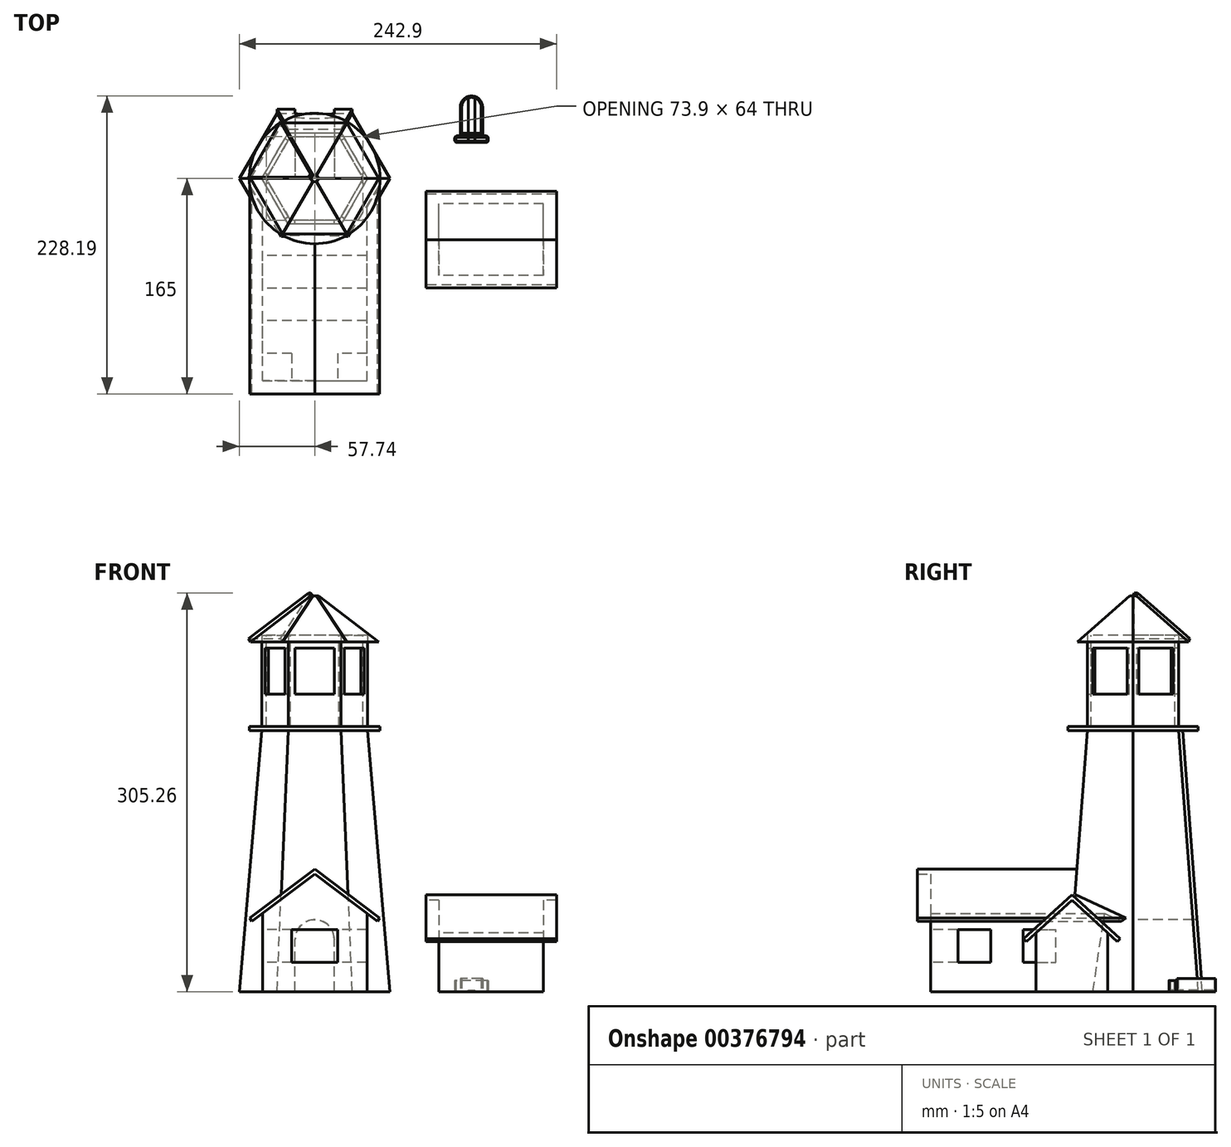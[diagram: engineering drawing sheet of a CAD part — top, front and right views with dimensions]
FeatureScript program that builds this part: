
annotation { "Feature Type Name" : "Feature", "Feature Type Description" : "" }
export const myFeature = defineFeature(function(context is Context, id is Id, definition is map)
    precondition{}
    {
        {
            var Q0;
            Q0=qCreatedBy(makeId("Top.planeOp"),FACE);
            var sketch = newSketch(context, id + "F0", { "sketchPlane" : qUnion([Q0])});
            skCircle(sketch, "E0.cCircle", {"center": v(0, 0) * mm, "radius": 50 * mm, "construction": true});
            skLineSegment(sketch, "E0.0", {"start": v(28.87, -50) * mm, "end": v(-28.87, -50) * mm});
            skLineSegment(sketch, "E0.1", {"start": v(-28.87, -50) * mm, "end": v(-57.74, 0) * mm});
            skLineSegment(sketch, "E0.2", {"start": v(-57.74, 0) * mm, "end": v(-28.87, 50) * mm});
            skLineSegment(sketch, "E0.3", {"start": v(-28.87, 50) * mm, "end": v(28.87, 50) * mm});
            skLineSegment(sketch, "E0.4", {"start": v(28.87, 50) * mm, "end": v(57.74, 0) * mm});
            skLineSegment(sketch, "E0.5", {"start": v(57.74, 0) * mm, "end": v(28.87, -50) * mm});
            skPoint(sketch, "E0.0.midPoint", {"position": v(0, -50) * mm});
            skSolve(sketch);
        }
        {
            var Q0;
            Q0=qCreatedBy(makeId("Top.planeOp"),FACE);
            cPlane(context, id + "F1", {"entities" : qUnion([Q0]), "cplaneType" : CPlaneType.OFFSET, "offset" : 200 * mm, "width" : 150 * mm, "height" : 150 * mm});
        }
        {
            var Q0;
            Q0=qCreatedBy(id+"F1.planeOp",FACE);
            var sketch = newSketch(context, id + "F2", { "sketchPlane" : qUnion([Q0])});
            skCircle(sketch, "E1.cCircle", {"center": v(0, 0) * mm, "radius": 35 * mm, "construction": true});
            skLineSegment(sketch, "E1.0", {"start": v(20.2, -35) * mm, "end": v(-20.2, -35) * mm});
            skLineSegment(sketch, "E1.1", {"start": v(-20.2, -35) * mm, "end": v(-40.41, 0) * mm});
            skLineSegment(sketch, "E1.2", {"start": v(-40.41, 0) * mm, "end": v(-20.2, 35) * mm});
            skLineSegment(sketch, "E1.3", {"start": v(-20.2, 35) * mm, "end": v(20.2, 35) * mm});
            skLineSegment(sketch, "E1.4", {"start": v(20.2, 35) * mm, "end": v(40.41, 0) * mm});
            skLineSegment(sketch, "E1.5", {"start": v(40.41, 0) * mm, "end": v(20.2, -35) * mm});
            skPoint(sketch, "E1.0.midPoint", {"position": v(0, -35) * mm});
            skSolve(sketch);
        }
        {
            var Q0;
            Q0=makeQuery(id+"F0.imprint","IMPRINT",FACE,{"disambiguationData":[TD([[makeQuery(id+"F0.imprint","IMPRINT",EDGE,{"derivedFrom":sQuery(id+"F0.wireOp",EDGE,"E0.0")}),-1.0]])]});
            var Q1;
            Q1=makeQuery(id+"F2.imprint","IMPRINT",FACE,{"disambiguationData":[TD([[makeQuery(id+"F2.imprint","IMPRINT",EDGE,{"derivedFrom":sQuery(id+"F2.wireOp",EDGE,"E1.0")}),-1.0]])]});
            loft(context, id + "F3", {"sheetProfilesArray" : [{ "sheetProfileEntities" : qUnion([Q0]) }, { "sheetProfileEntities" : qUnion([Q1]) }]});
        }
        {
            var Q0;
            Q0=makeQuery(id+"F3.opLoft","CAP_FACE",FACE,{"disambiguationData":[OSD([makeQuery(id+"F2.imprint","IMPRINT",FACE,{"disambiguationData":[TD([[makeQuery(id+"F2.imprint","IMPRINT",EDGE,{"derivedFrom":sQuery(id+"F2.wireOp",EDGE,"E1.0")}),-1.0]])]})])],"isStart":true});
            var sketch = newSketch(context, id + "F4", { "sketchPlane" : qUnion([Q0])});
            skCircle(sketch, "E2", {"center": v(0, 0) * mm, "radius": 50 * mm});
            skSolve(sketch);
        }
        {
            var Q0;
            Q0=makeQuery(id+"F4.imprint","IMPRINT",FACE,{"disambiguationData":[TD([[makeQuery(id+"F4.imprint","IMPRINT",EDGE,{"derivedFrom":sQuery(id+"F4.wireOp",EDGE,"E2")}),1.0]])]});
            var Q1;
            {var subQ2=sQuery(id+"F2.wireOp",EDGE,"E1.1");var subQ3=sQuery(id+"F2.wireOp",EDGE,"E1.0");var subQ4=sQuery(id+"F2.wireOp",EDGE,"E1.5");Q1=makeQuery(id+"F4.imprint","IMPRINT",FACE,{"disambiguationData":[TD([[makeQuery(id+"F4.imprint","IMPRINT",EDGE,{"derivedFrom":makeQuery(id+"F3.opLoft","MID_CAP_EDGE",EDGE,{"disambiguationData":[OSD([subQ3,subQ2,subQ4])],"capPos":1.0})}),1.0]])]});}
            extrude(context, id + "F5", {"entities" : qUnion([Q0, Q1]), "depth" : 3 * mm});
        }
        {
            var Q0;
            Q0=makeQuery(id+"F5.opExtrude","CAP_FACE",FACE,{"disambiguationData":[OSD([sQuery(id+"F4.wireOp",EDGE,"E2")])],"isStart":false});
            var sketch = newSketch(context, id + "F6", { "sketchPlane" : qUnion([Q0])});
            skCircle(sketch, "E3.cCircle", {"center": v(0, 0) * mm, "radius": 35 * mm, "construction": true});
            skLineSegment(sketch, "E3.0", {"start": v(20.2, -35) * mm, "end": v(-20.2, -35) * mm});
            skLineSegment(sketch, "E3.1", {"start": v(-20.2, -35) * mm, "end": v(-40.41, 0) * mm});
            skLineSegment(sketch, "E3.2", {"start": v(-40.41, 0) * mm, "end": v(-20.2, 35) * mm});
            skLineSegment(sketch, "E3.3", {"start": v(-20.2, 35) * mm, "end": v(20.2, 35) * mm});
            skLineSegment(sketch, "E3.4", {"start": v(20.2, 35) * mm, "end": v(40.41, 0) * mm});
            skLineSegment(sketch, "E3.5", {"start": v(40.41, 0) * mm, "end": v(20.2, -35) * mm});
            skPoint(sketch, "E3.0.midPoint", {"position": v(0, -35) * mm});
            skSolve(sketch);
        }
        {
            var Q0;
            Q0=makeQuery(id+"F6.imprint","IMPRINT",FACE,{"disambiguationData":[TD([[makeQuery(id+"F6.imprint","IMPRINT",EDGE,{"derivedFrom":sQuery(id+"F6.wireOp",EDGE,"E3.0")}),-1.0]])]});
            extrude(context, id + "F7", {"entities" : qUnion([Q0]), "depth" : 70 * mm});
        }
        {
            var Q0;
            Q0=makeQuery(id+"F7.opExtrude","CAP_FACE",FACE,{"disambiguationData":[OSD([sQuery(id+"F6.wireOp",EDGE,"E3.0"),sQuery(id+"F6.wireOp",EDGE,"E3.1"),sQuery(id+"F6.wireOp",EDGE,"E3.2"),sQuery(id+"F6.wireOp",EDGE,"E3.3"),sQuery(id+"F6.wireOp",EDGE,"E3.4"),sQuery(id+"F6.wireOp",EDGE,"E3.5")])],"isStart":false});
            var sketch = newSketch(context, id + "F8", { "sketchPlane" : qUnion([Q0])});
            skCircle(sketch, "E4.cCircle", {"center": v(0, 0) * mm, "radius": 32 * mm, "construction": true});
            skLineSegment(sketch, "E4.0", {"start": v(18.48, -32) * mm, "end": v(-18.48, -32) * mm});
            skLineSegment(sketch, "E4.1", {"start": v(-18.48, -32) * mm, "end": v(-36.95, 0) * mm});
            skLineSegment(sketch, "E4.2", {"start": v(-36.95, 0) * mm, "end": v(-18.48, 32) * mm});
            skLineSegment(sketch, "E4.3", {"start": v(-18.48, 32) * mm, "end": v(18.48, 32) * mm});
            skLineSegment(sketch, "E4.4", {"start": v(18.48, 32) * mm, "end": v(36.95, 0) * mm});
            skLineSegment(sketch, "E4.5", {"start": v(36.95, 0) * mm, "end": v(18.48, -32) * mm});
            skPoint(sketch, "E4.0.midPoint", {"position": v(0, -32) * mm});
            skSolve(sketch);
        }
        {
            var Q0;
            Q0=makeQuery(id+"F8.imprint","IMPRINT",FACE,{"disambiguationData":[TD([[makeQuery(id+"F8.imprint","IMPRINT",EDGE,{"derivedFrom":sQuery(id+"F8.wireOp",EDGE,"E4.0")}),-1.0]])]});
            var Q1;
            Q1=makeQuery(id+"F5.opExtrude","CAP_FACE",FACE,{"disambiguationData":[OSD([sQuery(id+"F4.wireOp",EDGE,"E2")])],"isStart":false});
            extrude(context, id + "F9", {"entities" : qUnion([Q0]), "operationType" : NewBodyOperationType.REMOVE, "endBound" : BoundingType.UP_TO_SURFACE, "oppositeDirection" : true, "endBoundEntityFace" : qUnion([Q1]), "depth" : 25 * mm});
        }
        {
            var Q0;
            Q0=makeQuery(id+"F7.opExtrude","CAP_FACE",FACE,{"disambiguationData":[OSD([sQuery(id+"F6.wireOp",EDGE,"E3.0"),sQuery(id+"F6.wireOp",EDGE,"E3.1"),sQuery(id+"F6.wireOp",EDGE,"E3.2"),sQuery(id+"F6.wireOp",EDGE,"E3.3"),sQuery(id+"F6.wireOp",EDGE,"E3.4"),sQuery(id+"F6.wireOp",EDGE,"E3.5")])],"isStart":false});
            var sketch = newSketch(context, id + "F10", { "sketchPlane" : qUnion([Q0])});
            skLineSegment(sketch, "E5", {"start": v(0, -32) * mm, "end": v(0, -35) * mm, "construction": true});
            skLineSegment(sketch, "E6.bottom", {"start": v(15.2, -35) * mm, "end": v(-15.2, -35) * mm});
            skLineSegment(sketch, "E6.top", {"start": v(15.2, -32) * mm, "end": v(-15.2, -32) * mm});
            skLineSegment(sketch, "E6.left", {"start": v(15.2, -35) * mm, "end": v(15.2, -32) * mm});
            skLineSegment(sketch, "E6.right", {"start": v(-15.2, -35) * mm, "end": v(-15.2, -32) * mm});
            skPoint(sketch, "E6.middle", {"position": v(0, -33.5) * mm});
            skLineSegment(sketch, "E7.1.0", {"start": v(35.32, -2.83) * mm, "end": v(20.1, -29.17) * mm});
            skLineSegment(sketch, "E7.1.1", {"start": v(37.91, -4.33) * mm, "end": v(35.32, -2.83) * mm});
            skLineSegment(sketch, "E7.1.2", {"start": v(37.91, -4.33) * mm, "end": v(22.7, -30.67) * mm});
            skLineSegment(sketch, "E7.1.3", {"start": v(22.7, -30.67) * mm, "end": v(20.1, -29.17) * mm});
            skLineSegment(sketch, "E7.2.0", {"start": v(20.1, 29.17) * mm, "end": v(35.32, 2.83) * mm});
            skLineSegment(sketch, "E7.2.1", {"start": v(22.7, 30.67) * mm, "end": v(20.1, 29.17) * mm});
            skLineSegment(sketch, "E7.2.2", {"start": v(22.7, 30.67) * mm, "end": v(37.91, 4.33) * mm});
            skLineSegment(sketch, "E7.2.3", {"start": v(37.91, 4.33) * mm, "end": v(35.32, 2.83) * mm});
            skLineSegment(sketch, "E7.3.0", {"start": v(-15.2, 32) * mm, "end": v(15.2, 32) * mm});
            skLineSegment(sketch, "E7.3.1", {"start": v(-15.2, 35) * mm, "end": v(-15.2, 32) * mm});
            skLineSegment(sketch, "E7.3.2", {"start": v(-15.2, 35) * mm, "end": v(15.2, 35) * mm});
            skLineSegment(sketch, "E7.3.3", {"start": v(15.2, 35) * mm, "end": v(15.2, 32) * mm});
            skLineSegment(sketch, "E7.4.0", {"start": v(-35.32, 2.83) * mm, "end": v(-20.1, 29.17) * mm});
            skLineSegment(sketch, "E7.4.1", {"start": v(-37.91, 4.33) * mm, "end": v(-35.32, 2.83) * mm});
            skLineSegment(sketch, "E7.4.2", {"start": v(-37.91, 4.33) * mm, "end": v(-22.7, 30.67) * mm});
            skLineSegment(sketch, "E7.4.3", {"start": v(-22.7, 30.67) * mm, "end": v(-20.1, 29.17) * mm});
            skLineSegment(sketch, "E7.5.0", {"start": v(-20.1, -29.17) * mm, "end": v(-35.32, -2.83) * mm});
            skLineSegment(sketch, "E7.5.1", {"start": v(-22.7, -30.67) * mm, "end": v(-20.1, -29.17) * mm});
            skLineSegment(sketch, "E7.5.2", {"start": v(-22.7, -30.67) * mm, "end": v(-37.91, -4.33) * mm});
            skLineSegment(sketch, "E7.5.3", {"start": v(-37.91, -4.33) * mm, "end": v(-35.32, -2.83) * mm});
            skPoint(sketch, "E7.center", {"position": v(0, 0) * mm});
            skSolve(sketch);
        }
        {
            var Q0;
            Q0 = qSketchRegion(id + "F10", true);
            extrude(context, id + "F11", {"entities" : qUnion([Q0]), "operationType" : NewBodyOperationType.REMOVE, "oppositeDirection" : true, "depth" : 45 * mm, "hasSecondDirection" : true, "secondDirectionOppositeDirection" : true, "secondDirectionDepth" : 10 * mm});
        }
        {
            var Q0;
            Q0=makeQuery(id+"F7.opExtrude","CAP_FACE",FACE,{"disambiguationData":[OSD([sQuery(id+"F6.wireOp",EDGE,"E3.0"),sQuery(id+"F6.wireOp",EDGE,"E3.1"),sQuery(id+"F6.wireOp",EDGE,"E3.2"),sQuery(id+"F6.wireOp",EDGE,"E3.3"),sQuery(id+"F6.wireOp",EDGE,"E3.4"),sQuery(id+"F6.wireOp",EDGE,"E3.5")])],"isStart":false});
            cPlane(context, id + "F12", {"entities" : qUnion([Q0]), "cplaneType" : CPlaneType.OFFSET, "offset" : 5 * mm, "oppositeDirection" : true, "width" : 150 * mm, "height" : 150 * mm});
        }
        {
            var Q0;
            Q0=qCreatedBy(id+"F12.planeOp",FACE);
            var sketch = newSketch(context, id + "F13", { "sketchPlane" : qUnion([Q0])});
            skCircle(sketch, "E8.cCircle", {"center": v(0, 0) * mm, "radius": 42.5 * mm, "construction": true});
            skLineSegment(sketch, "E8.0", {"start": v(24.54, -42.5) * mm, "end": v(-24.54, -42.5) * mm});
            skLineSegment(sketch, "E8.1", {"start": v(-24.54, -42.5) * mm, "end": v(-49.07, 0) * mm});
            skLineSegment(sketch, "E8.2", {"start": v(-49.07, 0) * mm, "end": v(-24.54, 42.5) * mm});
            skLineSegment(sketch, "E8.3", {"start": v(-24.54, 42.5) * mm, "end": v(24.54, 42.5) * mm});
            skLineSegment(sketch, "E8.4", {"start": v(24.54, 42.5) * mm, "end": v(49.07, 0) * mm});
            skLineSegment(sketch, "E8.5", {"start": v(49.07, 0) * mm, "end": v(24.54, -42.5) * mm});
            skPoint(sketch, "E8.0.midPoint", {"position": v(0, -42.5) * mm});
            skSolve(sketch);
        }
        {
            var Q0;
            Q0=qCreatedBy(id+"F12.planeOp",FACE);
            cPlane(context, id + "F14", {"entities" : qUnion([Q0]), "cplaneType" : CPlaneType.OFFSET, "offset" : 35 * mm, "width" : 150 * mm, "height" : 150 * mm});
        }
        {
            var Q0;
            Q0=qCreatedBy(id+"F14.planeOp",FACE);
            var sketch = newSketch(context, id + "F15", { "sketchPlane" : qUnion([Q0])});
            skCircle(sketch, "E9.cCircle", {"center": v(0, 0) * mm, "radius": 2.5 * mm, "construction": true});
            skLineSegment(sketch, "E9.0", {"start": v(1.44, -2.5) * mm, "end": v(-1.44, -2.5) * mm});
            skLineSegment(sketch, "E9.1", {"start": v(-1.44, -2.5) * mm, "end": v(-2.89, 0) * mm});
            skLineSegment(sketch, "E9.2", {"start": v(-2.89, 0) * mm, "end": v(-1.44, 2.5) * mm});
            skLineSegment(sketch, "E9.3", {"start": v(-1.44, 2.5) * mm, "end": v(1.44, 2.5) * mm});
            skLineSegment(sketch, "E9.4", {"start": v(1.44, 2.5) * mm, "end": v(2.89, 0) * mm});
            skLineSegment(sketch, "E9.5", {"start": v(2.89, 0) * mm, "end": v(1.44, -2.5) * mm});
            skPoint(sketch, "E9.0.midPoint", {"position": v(0, -2.5) * mm});
            skSolve(sketch);
        }
        {
            var Q1;
            Q1=makeQuery(id+"F13.imprint","IMPRINT",FACE,{"disambiguationData":[TD([[makeQuery(id+"F13.imprint","IMPRINT",EDGE,{"derivedFrom":sQuery(id+"F13.wireOp",EDGE,"E8.0")}),-1.0]])]});
            var Q2;
            Q2=makeQuery(id+"F15.imprint","IMPRINT",FACE,{"disambiguationData":[TD([[makeQuery(id+"F15.imprint","IMPRINT",EDGE,{"derivedFrom":sQuery(id+"F15.wireOp",EDGE,"E9.0")}),-1.0]])]});
            loft(context, id + "F16", {"sheetProfilesArray" : [{ "sheetProfileEntities" : qUnion([Q1]) }, { "sheetProfileEntities" : qUnion([Q2]) }]});
        }
        {
            var Q0;
            Q0=qCreatedBy(makeId("Top.planeOp"),FACE);
            var sketch = newSketch(context, id + "F17", { "sketchPlane" : qUnion([Q0])});
            skLineSegment(sketch, "E10", {"start": v(0, 0) * mm, "end": v(0, -80) * mm, "construction": true});
            skLineSegment(sketch, "E11.bottom", {"start": v(-40, -155) * mm, "end": v(40, -155) * mm});
            skLineSegment(sketch, "E11.top", {"start": v(-40, -5) * mm, "end": v(40, -5) * mm});
            skLineSegment(sketch, "E11.left", {"start": v(-40, -155) * mm, "end": v(-40, -5) * mm});
            skLineSegment(sketch, "E11.right", {"start": v(40, -155) * mm, "end": v(40, -5) * mm});
            skPoint(sketch, "E11.middle", {"position": v(0, -80) * mm});
            skSolve(sketch);
        }
        {
            var Q0;
            Q0 = qSketchRegion(id + "F17", true);
            extrude(context, id + "F18", {"entities" : qUnion([Q0]), "operationType" : NewBodyOperationType.ADD, "depth" : 60 * mm});
        }
        {
            var Q0;
            Q0=makeQuery(id+"F18.opExtrude","SWEPT_FACE",FACE,{"disambiguationData":[OSD([sQuery(id+"F17.wireOp",EDGE,"E11.bottom")])]});
            var sketch = newSketch(context, id + "F19", { "sketchPlane" : qUnion([Q0])});
            skLineSegment(sketch, "E12", {"start": v(0, 60) * mm, "end": v(0, 90) * mm, "construction": true});
            skPoint(sketch, "E12.endSnap0", {"position": v(-20, 75) * mm});
            skLineSegment(sketch, "E13", {"start": v(0, 90) * mm, "end": v(-40, 60) * mm});
            skLineSegment(sketch, "E14", {"start": v(0, 90) * mm, "end": v(40, 60) * mm});
            skSolve(sketch);
        }
        {
            var Q0;
            Q0=makeQuery(id+"F19.imprint","IMPRINT",FACE,{"disambiguationData":[TD([[makeQuery(id+"F19.imprint","IMPRINT",EDGE,{"derivedFrom":sQuery(id+"F19.wireOp",EDGE,"E13")}),1.0]])]});
            extrude(context, id + "F20", {"entities" : qUnion([Q0]), "operationType" : NewBodyOperationType.ADD, "oppositeDirection" : true, "depth" : 150 * mm});
        }
        {
            var Q0;
            {var subQ0=sQuery(id+"F17.wireOp",EDGE,"E11.right");Q0=makeQuery(id+"F20.boolean.opBoolean","MERGE",FACE,{"derivedFrom":[makeQuery(id+"F18.opExtrude","SWEPT_FACE",FACE,{"disambiguationData":[OSD([subQ0])]}),makeQuery(id+"F20.opExtrude","CAP_FACE",FACE,{"disambiguationData":[OSD([subQ0,sQuery(id+"F19.wireOp",EDGE,"E13"),sQuery(id+"F19.wireOp",EDGE,"E14")])],"isStart":true})]});}
            var sketch = newSketch(context, id + "F21", { "sketchPlane" : qUnion([Q0])});
            skLineSegment(sketch, "E15", {"start": v(0, 90) * mm, "end": v(0, 93.75) * mm});
            skLineSegment(sketch, "E16", {"start": v(0, 93.75) * mm, "end": v(-49.8, 56.4) * mm});
            skLineSegment(sketch, "E17", {"start": v(-49.8, 56.4) * mm, "end": v(-48, 54) * mm});
            skLineSegment(sketch, "E18", {"start": v(-48, 54) * mm, "end": v(-40, 60) * mm});
            skLineSegment(sketch, "E19.MirrorCS", {"start": v(0, 93.75) * mm, "end": v(49.8, 56.4) * mm});
            skLineSegment(sketch, "E20.MirrorCS", {"start": v(49.8, 56.4) * mm, "end": v(48, 54) * mm});
            skLineSegment(sketch, "E21.MirrorCS", {"start": v(48, 54) * mm, "end": v(40, 60) * mm});
            skSolve(sketch);
        }
        {
            var Q0;
            Q0=makeQuery(id+"F21.imprint","IMPRINT",FACE,{"disambiguationData":[TD([[makeQuery(id+"F21.imprint","IMPRINT",EDGE,{"derivedFrom":sQuery(id+"F21.wireOp",EDGE,"E15")}),1.0]])]});
            var Q1;
            Q1=makeQuery(id+"F21.imprint","IMPRINT",FACE,{"disambiguationData":[TD([[makeQuery(id+"F21.imprint","IMPRINT",EDGE,{"derivedFrom":sQuery(id+"F21.wireOp",EDGE,"E15")}),-1.0]])]});
            extrude(context, id + "F22", {"entities" : qUnion([Q0, Q1]), "operationType" : NewBodyOperationType.ADD, "depth" : 10 * mm, "hasSecondDirection" : true, "secondDirectionOppositeDirection" : true, "secondDirectionDepth" : 150 * mm});
        }
        {
            var Q0;
            Q0=qCreatedBy(makeId("Front.planeOp"),FACE);
            var sketch = newSketch(context, id + "F23", { "sketchPlane" : qUnion([Q0])});
            skLineSegment(sketch, "E22", {"start": v(0, 0) * mm, "end": v(0, 20) * mm, "construction": true});
            skLineSegment(sketch, "E23.bottom", {"start": v(15, 0) * mm, "end": v(-15, 0) * mm});
            skLineSegment(sketch, "E23.top", {"start": v(15, 40) * mm, "end": v(-15, 40) * mm});
            skLineSegment(sketch, "E23.left", {"start": v(15, 0) * mm, "end": v(15, 40) * mm});
            skLineSegment(sketch, "E23.right", {"start": v(-15, 0) * mm, "end": v(-15, 40) * mm});
            skPoint(sketch, "E23.middle", {"position": v(0, 20) * mm});
            skArc(sketch, "E24", {"start": v(15, 40) * mm, "mid": v(0, 55) * mm, "end": v(-15, 40) * mm});
            skSolve(sketch);
        }
        {
            var Q0;
            Q0 = qSketchRegion(id + "F23", true);
            extrude(context, id + "F24", {"entities" : qUnion([Q0]), "operationType" : NewBodyOperationType.REMOVE, "endBound" : BoundingType.THROUGH_ALL, "oppositeDirection" : true, "depth" : 25 * mm});
        }
        {
            var Q0;
            Q0=makeQuery(id+"F18.opExtrude","SWEPT_FACE",FACE,{"disambiguationData":[OSD([sQuery(id+"F17.wireOp",EDGE,"E11.left")])]});
            var sketch = newSketch(context, id + "F25", { "sketchPlane" : qUnion([Q0])});
            skLineSegment(sketch, "E25.bottom", {"start": v(84, 22.5) * mm, "end": v(59, 22.5) * mm});
            skLineSegment(sketch, "E25.top", {"start": v(84, 47.5) * mm, "end": v(59, 47.5) * mm});
            skLineSegment(sketch, "E25.left", {"start": v(84, 22.5) * mm, "end": v(84, 47.5) * mm});
            skLineSegment(sketch, "E25.right", {"start": v(59, 22.5) * mm, "end": v(59, 47.5) * mm});
            skPoint(sketch, "E25.middle", {"position": v(71.5, 35) * mm});
            skLineSegment(sketch, "E26.1.0.0", {"start": v(109, 22.5) * mm, "end": v(109, 47.5) * mm});
            skLineSegment(sketch, "E26.1.0.1", {"start": v(134, 47.5) * mm, "end": v(109, 47.5) * mm});
            skLineSegment(sketch, "E26.1.0.2", {"start": v(134, 22.5) * mm, "end": v(134, 47.5) * mm});
            skLineSegment(sketch, "E26.1.0.3", {"start": v(134, 22.5) * mm, "end": v(109, 22.5) * mm});
            skLineSegment(sketch, "E26.direction1", {"start": v(59, 22.5) * mm, "end": v(109, 22.5) * mm, "construction": true});
            skSolve(sketch);
        }
        {
            var Q0;
            Q0=makeQuery(id+"F25.imprint","IMPRINT",FACE,{"disambiguationData":[TD([[makeQuery(id+"F25.imprint","IMPRINT",EDGE,{"derivedFrom":sQuery(id+"F25.wireOp",EDGE,"E25.bottom")}),-1.0]])]});
            var Q1;
            Q1=makeQuery(id+"F25.imprint","IMPRINT",FACE,{"disambiguationData":[TD([[makeQuery(id+"F25.imprint","IMPRINT",EDGE,{"derivedFrom":sQuery(id+"F25.wireOp",EDGE,"E26.1.0.0")}),-1.0]])]});
            extrude(context, id + "F26", {"entities" : qUnion([Q0, Q1]), "operationType" : NewBodyOperationType.REMOVE, "endBound" : BoundingType.THROUGH_ALL, "oppositeDirection" : true, "depth" : 25 * mm});
        }
        {
            var Q0;
            {var subQ0=sQuery(id+"F17.wireOp",EDGE,"E11.bottom");Q0=makeQuery(id+"F20.boolean.opBoolean","MERGE",FACE,{"derivedFrom":[makeQuery(id+"F18.opExtrude","SWEPT_FACE",FACE,{"disambiguationData":[OSD([subQ0])]}),makeQuery(id+"F20.opExtrude","CAP_FACE",FACE,{"disambiguationData":[OSD([subQ0,sQuery(id+"F19.wireOp",EDGE,"E13"),sQuery(id+"F19.wireOp",EDGE,"E14")])],"isStart":true})]});}
            var sketch = newSketch(context, id + "F27", { "sketchPlane" : qUnion([Q0])});
            skLineSegment(sketch, "E27", {"start": v(0, 0) * mm, "end": v(0, 35) * mm, "construction": true});
            skPoint(sketch, "E27.endSnap0", {"position": v(0, 0) * mm});
            skLineSegment(sketch, "E28.bottom", {"start": v(-17.5, 47.5) * mm, "end": v(17.5, 47.5) * mm});
            skLineSegment(sketch, "E28.top", {"start": v(-17.5, 22.5) * mm, "end": v(17.5, 22.5) * mm});
            skLineSegment(sketch, "E28.left", {"start": v(-17.5, 47.5) * mm, "end": v(-17.5, 22.5) * mm});
            skLineSegment(sketch, "E28.right", {"start": v(17.5, 47.5) * mm, "end": v(17.5, 22.5) * mm});
            skPoint(sketch, "E28.middle", {"position": v(0, 35) * mm});
            skSolve(sketch);
        }
        {
            var Q0;
            Q0=makeQuery(id+"F27.imprint","IMPRINT",FACE,{"disambiguationData":[TD([[makeQuery(id+"F27.imprint","IMPRINT",EDGE,{"derivedFrom":sQuery(id+"F27.wireOp",EDGE,"E28.bottom")}),-1.0]])]});
            extrude(context, id + "F28", {"entities" : qUnion([Q0]), "operationType" : NewBodyOperationType.REMOVE, "oppositeDirection" : true, "depth" : 25 * mm});
        }
        {
            var Q0;
            Q0=qCreatedBy(makeId("Top.planeOp"),FACE);
            var sketch = newSketch(context, id + "F29", { "sketchPlane" : qUnion([Q0])});
            skLineSegment(sketch, "E29.bottom", {"start": v(175.16, -74.3) * mm, "end": v(95.16, -74.3) * mm});
            skLineSegment(sketch, "E29.top", {"start": v(175.16, -19.3) * mm, "end": v(95.16, -19.3) * mm});
            skLineSegment(sketch, "E29.left", {"start": v(175.16, -74.3) * mm, "end": v(175.16, -19.3) * mm});
            skLineSegment(sketch, "E29.right", {"start": v(95.16, -74.3) * mm, "end": v(95.16, -19.3) * mm});
            skPoint(sketch, "E29.middle", {"position": v(135.16, -46.8) * mm});
            skSolve(sketch);
        }
        {
            var Q0;
            Q0=makeQuery(id+"F29.imprint","IMPRINT",FACE,{"disambiguationData":[TD([[makeQuery(id+"F29.imprint","IMPRINT",EDGE,{"derivedFrom":sQuery(id+"F29.wireOp",EDGE,"E29.bottom")}),-1.0]])]});
            extrude(context, id + "F30", {"entities" : qUnion([Q0]), "depth" : 45 * mm});
        }
        {
            var Q0;
            Q0=makeQuery(id+"F30.opExtrude","SWEPT_FACE",FACE,{"disambiguationData":[OSD([sQuery(id+"F29.wireOp",EDGE,"E29.left")])]});
            var sketch = newSketch(context, id + "F31", { "sketchPlane" : qUnion([Q0])});
            skLineSegment(sketch, "E30", {"start": v(-46.8, 45) * mm, "end": v(-46.8, 70) * mm, "construction": true});
            skLineSegment(sketch, "E31", {"start": v(-46.8, 70) * mm, "end": v(-74.3, 45) * mm});
            skLineSegment(sketch, "E32", {"start": v(-46.8, 70) * mm, "end": v(-19.3, 45) * mm});
            skSolve(sketch);
        }
        {
            var Q0;
            Q0=makeQuery(id+"F31.imprint","IMPRINT",FACE,{"disambiguationData":[TD([[makeQuery(id+"F31.imprint","IMPRINT",EDGE,{"derivedFrom":sQuery(id+"F31.wireOp",EDGE,"E31")}),1.0]])]});
            var Q1;
            Q1=makeQuery(id+"F30.opExtrude","SWEPT_FACE",FACE,{"disambiguationData":[OSD([sQuery(id+"F29.wireOp",EDGE,"E29.right")])]});
            extrude(context, id + "F32", {"entities" : qUnion([Q0]), "operationType" : NewBodyOperationType.ADD, "endBound" : BoundingType.UP_TO_SURFACE, "oppositeDirection" : true, "endBoundEntityFace" : qUnion([Q1]), "depth" : 25 * mm});
        }
        {
            var Q0;
            {var subQ0=sQuery(id+"F29.wireOp",EDGE,"E29.left");Q0=makeQuery(id+"F32.boolean.opBoolean","MERGE",FACE,{"derivedFrom":[makeQuery(id+"F30.opExtrude","SWEPT_FACE",FACE,{"disambiguationData":[OSD([subQ0])]}),makeQuery(id+"F32.opExtrude","CAP_FACE",FACE,{"disambiguationData":[OSD([subQ0,sQuery(id+"F31.wireOp",EDGE,"E31"),sQuery(id+"F31.wireOp",EDGE,"E32")])],"isStart":true})]});}
            var sketch = newSketch(context, id + "F33", { "sketchPlane" : qUnion([Q0])});
            skLineSegment(sketch, "E33", {"start": v(-46.8, 70) * mm, "end": v(-46.8, 74.05) * mm});
            skLineSegment(sketch, "E34", {"start": v(-46.8, 74.05) * mm, "end": v(-83.7, 40.5) * mm});
            skLineSegment(sketch, "E35", {"start": v(-83.7, 40.5) * mm, "end": v(-81.7, 38.27) * mm});
            skLineSegment(sketch, "E36", {"start": v(-81.7, 38.27) * mm, "end": v(-74.3, 45) * mm});
            skLineSegment(sketch, "E37.MirrorCS", {"start": v(-46.8, 74.05) * mm, "end": v(-9.87, 40.5) * mm});
            skLineSegment(sketch, "E38.MirrorCS", {"start": v(-9.87, 40.5) * mm, "end": v(-11.9, 38.27) * mm});
            skLineSegment(sketch, "E39.MirrorCS", {"start": v(-11.9, 38.27) * mm, "end": v(-19.3, 45) * mm});
            skSolve(sketch);
        }
        {
            var Q0;
            Q0=makeQuery(id+"F33.imprint","IMPRINT",FACE,{"disambiguationData":[TD([[makeQuery(id+"F33.imprint","IMPRINT",EDGE,{"derivedFrom":sQuery(id+"F33.wireOp",EDGE,"E33")}),1.0]])]});
            var Q1;
            Q1=makeQuery(id+"F33.imprint","IMPRINT",FACE,{"disambiguationData":[TD([[makeQuery(id+"F33.imprint","IMPRINT",EDGE,{"derivedFrom":sQuery(id+"F33.wireOp",EDGE,"E33")}),-1.0]])]});
            extrude(context, id + "F34", {"entities" : qUnion([Q0, Q1]), "operationType" : NewBodyOperationType.ADD, "depth" : 10 * mm, "hasSecondDirection" : true, "secondDirectionOppositeDirection" : true, "secondDirectionDepth" : 90 * mm});
        }
        {
            var Q0;
            Q0=qCreatedBy(makeId("Top.planeOp"),FACE);
            var sketch = newSketch(context, id + "F35", { "sketchPlane" : qUnion([Q0])});
            skLineSegment(sketch, "E40.bottom", {"start": v(127.56, 34.64) * mm, "end": v(112.56, 34.64) * mm});
            skLineSegment(sketch, "E40.top", {"start": v(127.56, 54.64) * mm, "end": v(112.56, 54.64) * mm});
            skLineSegment(sketch, "E40.left", {"start": v(127.56, 34.64) * mm, "end": v(127.56, 54.64) * mm});
            skLineSegment(sketch, "E40.right", {"start": v(112.56, 34.64) * mm, "end": v(112.56, 54.64) * mm});
            skPoint(sketch, "E40.middle", {"position": v(120.06, 44.64) * mm});
            skArc(sketch, "E41", {"start": v(112.56, 54.64) * mm, "mid": v(120.06, 62.14) * mm, "end": v(127.56, 54.64) * mm});
            skArc(sketch, "E42.0", {"start": v(111.51, 54.64) * mm, "mid": v(120.06, 63.19) * mm, "end": v(128.61, 54.64) * mm});
            skLineSegment(sketch, "E42.1", {"start": v(111.51, 33.59) * mm, "end": v(111.51, 54.64) * mm});
            skLineSegment(sketch, "E42.2", {"start": v(128.61, 33.59) * mm, "end": v(111.51, 33.59) * mm});
            skLineSegment(sketch, "E42.3", {"start": v(128.61, 33.59) * mm, "end": v(128.61, 54.64) * mm});
            skLineSegment(sketch, "E43", {"start": v(120.06, 44.64) * mm, "end": v(120.06, 30.09) * mm, "construction": true});
            skLineSegment(sketch, "E44.bottom", {"start": v(130.94, 28.59) * mm, "end": v(109.19, 28.59) * mm});
            skLineSegment(sketch, "E44.top", {"start": v(130.94, 31.59) * mm, "end": v(109.19, 31.59) * mm});
            skLineSegment(sketch, "E44.left", {"start": v(131.94, 29.59) * mm, "end": v(131.94, 30.59) * mm});
            skLineSegment(sketch, "E44.right", {"start": v(108.19, 29.59) * mm, "end": v(108.19, 30.59) * mm});
            skPoint(sketch, "E44.middle", {"position": v(120.06, 30.09) * mm});
            skPoint(sketch, "E45.visualSharp", {"position": v(108.19, 31.59) * mm});
            skArc(sketch, "E45.filletArc", {"start": v(109.19, 31.59) * mm, "mid": v(108.48, 31.3) * mm, "end": v(108.19, 30.59) * mm});
            skPoint(sketch, "E46.visualSharp", {"position": v(131.94, 31.59) * mm});
            skArc(sketch, "E46.filletArc", {"start": v(131.94, 30.59) * mm, "mid": v(131.65, 31.3) * mm, "end": v(130.94, 31.59) * mm});
            skPoint(sketch, "E47.visualSharp", {"position": v(131.94, 28.59) * mm});
            skArc(sketch, "E47.filletArc", {"start": v(130.94, 28.59) * mm, "mid": v(131.65, 28.88) * mm, "end": v(131.94, 29.59) * mm});
            skPoint(sketch, "E48.visualSharp", {"position": v(108.19, 28.59) * mm});
            skArc(sketch, "E48.filletArc", {"start": v(108.19, 29.59) * mm, "mid": v(108.48, 28.88) * mm, "end": v(109.19, 28.59) * mm});
            skArc(sketch, "E49.0", {"start": v(133, 30.59) * mm, "mid": v(132.4, 32.04) * mm, "end": v(130.94, 32.64) * mm});
            skLineSegment(sketch, "E49.1", {"start": v(133, 29.59) * mm, "end": v(133, 30.59) * mm});
            skLineSegment(sketch, "E49.2", {"start": v(130.94, 32.64) * mm, "end": v(109.19, 32.64) * mm});
            skArc(sketch, "E49.3", {"start": v(130.94, 27.54) * mm, "mid": v(132.4, 28.14) * mm, "end": v(133, 29.59) * mm});
            skArc(sketch, "E49.4", {"start": v(109.19, 32.64) * mm, "mid": v(107.74, 32.04) * mm, "end": v(107.14, 30.59) * mm});
            skLineSegment(sketch, "E49.5", {"start": v(107.14, 29.59) * mm, "end": v(107.14, 30.59) * mm});
            skArc(sketch, "E49.6", {"start": v(107.14, 29.59) * mm, "mid": v(107.74, 28.14) * mm, "end": v(109.19, 27.54) * mm});
            skLineSegment(sketch, "E49.7", {"start": v(130.94, 27.54) * mm, "end": v(109.19, 27.54) * mm});
            skSolve(sketch);
        }
        {
            var Q0;
            Q0=makeQuery(id+"F35.imprint","IMPRINT",FACE,{"disambiguationData":[TD([[makeQuery(id+"F35.imprint","IMPRINT",EDGE,{"derivedFrom":sQuery(id+"F35.wireOp",EDGE,"E40.bottom")}),1.0]])]});
            extrude(context, id + "F36", {"entities" : qUnion([Q0]), "depth" : 10 * mm});
        }
        {
            var Q0;
            Q0=makeQuery(id+"F35.imprint","IMPRINT",FACE,{"disambiguationData":[TD([[makeQuery(id+"F35.imprint","IMPRINT",EDGE,{"derivedFrom":sQuery(id+"F35.wireOp",EDGE,"E44.bottom")}),1.0]])]});
            extrude(context, id + "F37", {"entities" : qUnion([Q0]), "depth" : 8.5 * mm});
        }
        {
            var Q0;
            Q0=makeQuery(id+"F36.opExtrude","CAP_FACE",FACE,{"disambiguationData":[OSD([sQuery(id+"F35.wireOp",EDGE,"E40.bottom"),sQuery(id+"F35.wireOp",EDGE,"E40.left"),sQuery(id+"F35.wireOp",EDGE,"E40.right"),sQuery(id+"F35.wireOp",EDGE,"E41"),sQuery(id+"F35.wireOp",EDGE,"E42.0"),sQuery(id+"F35.wireOp",EDGE,"E42.1"),sQuery(id+"F35.wireOp",EDGE,"E42.2"),sQuery(id+"F35.wireOp",EDGE,"E42.3")])],"isStart":true});
            var sketch = newSketch(context, id + "F38", { "sketchPlane" : qUnion([Q0])});
            skLineSegment(sketch, "E50", {"start": v(120.06, -33.59) * mm, "end": v(120.06, -45.4) * mm, "construction": true});
            skLineSegment(sketch, "E51.bottom", {"start": v(117.56, -62.4) * mm, "end": v(122.56, -62.4) * mm});
            skLineSegment(sketch, "E51.top", {"start": v(117.56, -28.4) * mm, "end": v(122.56, -28.4) * mm});
            skLineSegment(sketch, "E51.left", {"start": v(117.56, -62.4) * mm, "end": v(117.56, -28.4) * mm});
            skLineSegment(sketch, "E51.right", {"start": v(122.56, -62.4) * mm, "end": v(122.56, -28.4) * mm});
            skPoint(sketch, "E51.middle", {"position": v(120.06, -45.4) * mm});
            skSolve(sketch);
        }
        {
            var Q0;
            Q0 = qSketchRegion(id + "F38", true);
            extrude(context, id + "F39", {"entities" : qUnion([Q0]), "operationType" : NewBodyOperationType.ADD, "oppositeDirection" : true, "depth" : 1 * mm});
        }
        {
            var Q0;
            Q0=makeQuery(id+"F3.opLoft","SWEPT_FACE",FACE,{"disambiguationData":[OSD([sQuery(id+"F0.wireOp",EDGE,"E0.2"),sQuery(id+"F0.wireOp",EDGE,"E0.3"),sQuery(id+"F0.wireOp",EDGE,"E0.4"),sQuery(id+"F2.wireOp",EDGE,"E1.2"),sQuery(id+"F2.wireOp",EDGE,"E1.3"),sQuery(id+"F2.wireOp",EDGE,"E1.4")])]});
            extrude(context, id + "F40", {"entities" : qUnion([Q0]), "depth" : 3 * mm});
        }
        {
            var Q0;
            Q0=makeQuery(id+"F16.opLoft","SWEPT_FACE",FACE,{"disambiguationData":[OSD([sQuery(id+"F13.wireOp",EDGE,"E8.1"),sQuery(id+"F13.wireOp",EDGE,"E8.2"),sQuery(id+"F13.wireOp",EDGE,"E8.3"),sQuery(id+"F15.wireOp",EDGE,"E9.1"),sQuery(id+"F15.wireOp",EDGE,"E9.2"),sQuery(id+"F15.wireOp",EDGE,"E9.3")])]});
            extrude(context, id + "F41", {"entities" : qUnion([Q0]), "depth" : 3 * mm});
        }
    });
